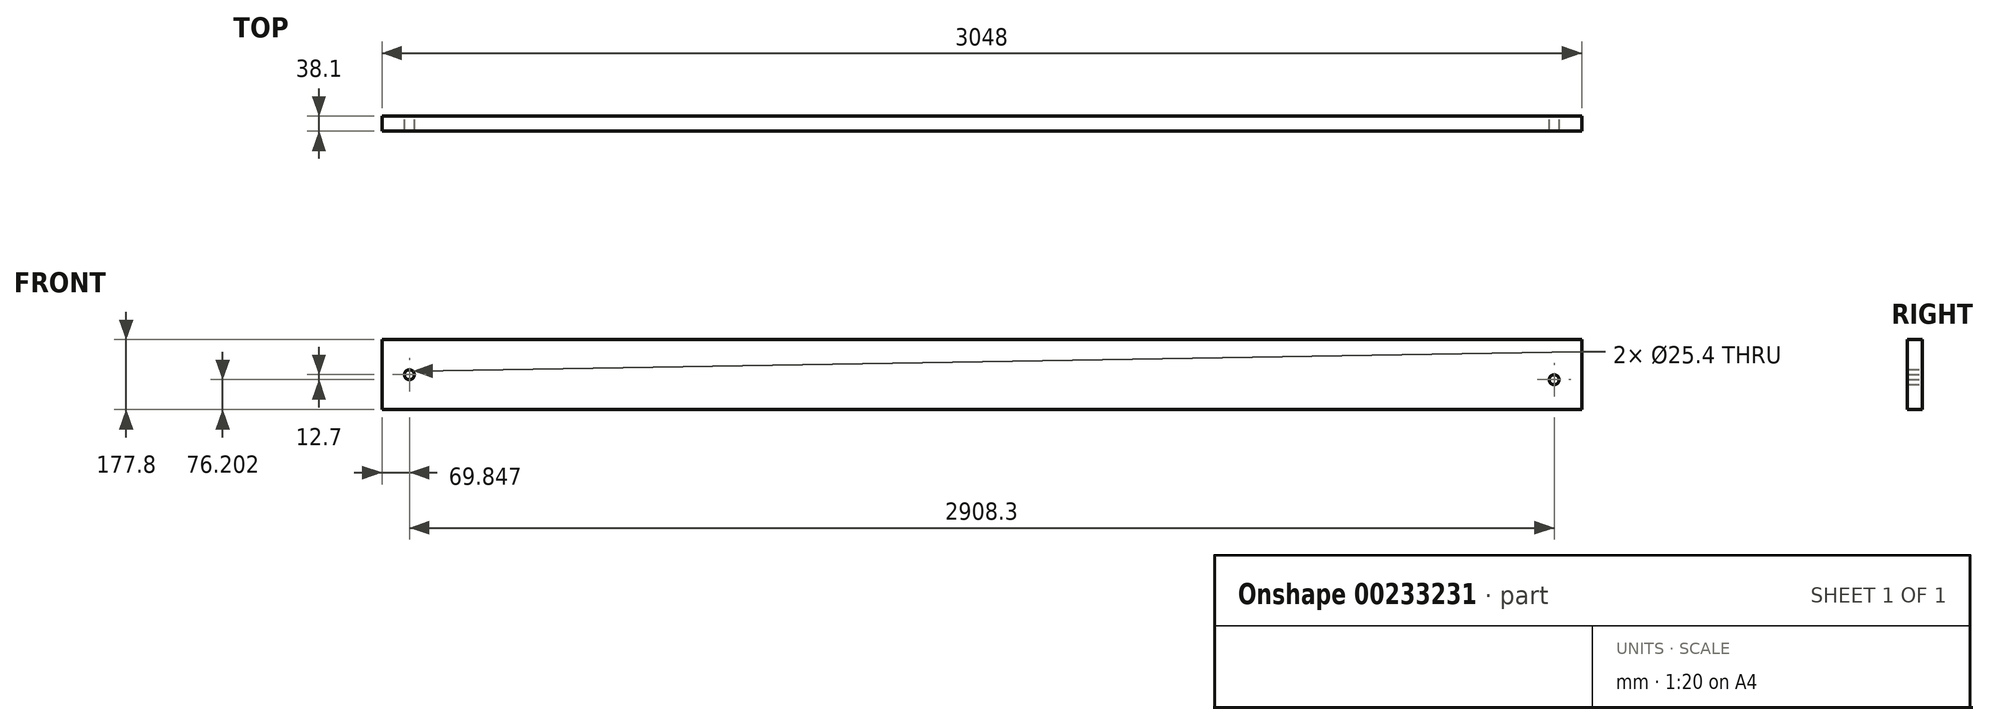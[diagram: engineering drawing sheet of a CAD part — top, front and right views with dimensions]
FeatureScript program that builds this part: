
annotation { "Feature Type Name" : "Feature", "Feature Type Description" : "" }
export const myFeature = defineFeature(function(context is Context, id is Id, definition is map)
    precondition{}
    {
        {
            var Q0;
            Q0=qCreatedBy(makeId("Front.planeOp"),FACE);
            var sketch = newSketch(context, id + "F0", { "sketchPlane" : qUnion([Q0])});
            skLineSegment(sketch, "E0.bottom", {"start": v(-1812.26, -1289.26) * mm, "end": v(1235.74, -1289.26) * mm});
            skLineSegment(sketch, "E0.top", {"start": v(-1812.26, -1467.06) * mm, "end": v(1235.74, -1467.06) * mm});
            skLineSegment(sketch, "E0.left", {"start": v(-1812.26, -1289.26) * mm, "end": v(-1812.26, -1467.06) * mm});
            skLineSegment(sketch, "E0.right", {"start": v(1235.74, -1289.26) * mm, "end": v(1235.74, -1467.06) * mm});
            skCircle(sketch, "E1", {"center": v(-1742.41, -1378.16) * mm, "radius": 12.7 * mm});
            skCircle(sketch, "E2", {"center": v(1165.89, -1390.86) * mm, "radius": 12.7 * mm});
            skSolve(sketch);
        }
        {
            var Q0;
            Q0=makeQuery(id+"F0.imprint","IMPRINT",FACE,{"disambiguationData":[TD([[makeQuery(id+"F0.imprint","IMPRINT",EDGE,{"derivedFrom":sQuery(id+"F0.wireOp",EDGE,"E0.bottom")}),-1.0]])]});
            extrude(context, id + "F1", {"entities" : qUnion([Q0]), "depth" : 38.1 * mm});
        }
    });
